# Revit family: BIMLIB_Конвектор_ВстраиваемыйВПолЭлектрическийСПринудительнойКонвекцией_ВКВЭ80_VITRON
name_source: partatom
category: Оборудование
revit_build: Autodesk Revit 2017 (Build: 20190508_0315(x64)
units: mm (PartAtom-declared; Revit-internal decimal feet)

## family parameters
Всегда вертикально = Да
На основе рабочей плоскости = Нет
Общий = Нет
При загрузке вырезать с полостями = Нет
Размер круглого соединителя = Использовать диаметр
Тип детали = Нормальный
Точка расчета площади = Нет

## types (1)
- Конвектор_Шириной 260мм
    1 = 1
    2 = 2
    3 = 3
    ADSK_URL документации изделия = https://vitron.ru
    ADSK_URL страницы изделия = https://vitron.ru
    ADSK_Версия Revit = 2017
    ADSK_Единица измерения = шт.
    ADSK_Завод-изготовитель = Вилма / VITRON
    ADSK_Классификация нагрузок = Прочее
    ADSK_Количество фаз = 1
    ADSK_Коэффициент мощности = 0.98
    ADSK_Обозначение = ВКВЭ.80.260
    ADSK_Размер_Высота = 80 мм
    ADSK_Размер_Диаметр = 15 мм
    ADSK_Размер_Ширина = 260 мм
    BL_BIM library = https://bimlib.pro
    URL = https://vitron.ru
    VIT_Степень защиты вентилятора = IP20
    VIT_Уровень звукового давления от вентилятора = 19/30 дБ(А)
    Изготовитель = Вилма / VITRON
    Материал_Корпуса = BIMLIB_ОцинкованнаяСталь_VITRON
    Материал_Решетка = BIMLIB_Алюминий_VITRON
    Описание = Встраиваемый в конструкцию пола электрический конвектор VITRON – это отопительный прибор, где в
качестве нагревательного элемента используются терморезисторы. Он предназначен для использования как
вспомогательный отопительный прибор с системами водяного отопления, системами теплого пола, так и в
качестве основного источника тепла, в местах где нет возможности использовать системы водяного отопления.
Допускается использовать в качестве основного отопительного прибора в помещениях с любыми потребностями
в интенсивности отопления.
